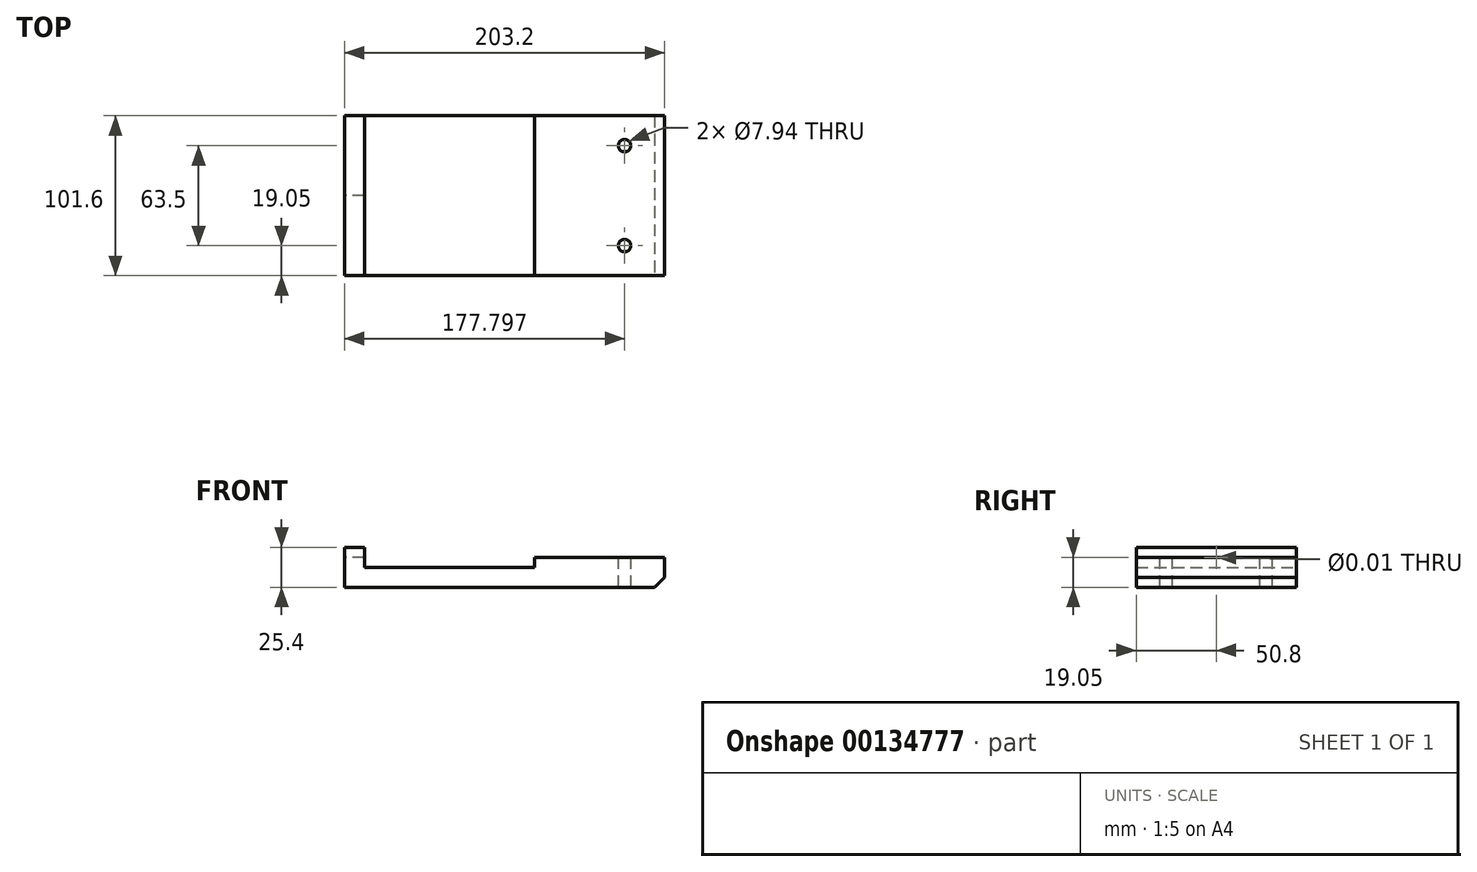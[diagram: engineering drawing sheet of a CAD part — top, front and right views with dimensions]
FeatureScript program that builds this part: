
annotation { "Feature Type Name" : "Feature", "Feature Type Description" : "" }
export const myFeature = defineFeature(function(context is Context, id is Id, definition is map)
    precondition{}
    {
        {
            var Q0;
            Q0=qCreatedBy(makeId("Front.planeOp"),FACE);
            var sketch = newSketch(context, id + "F0", { "sketchPlane" : qUnion([Q0])});
            skLineSegment(sketch, "E0", {"start": v(-106, -12.7) * mm, "end": v(97.2, -12.7) * mm});
            skLineSegment(sketch, "E1", {"start": v(97.2, -12.7) * mm, "end": v(97.2, 6.35) * mm});
            skLineSegment(sketch, "E2", {"start": v(97.2, 6.35) * mm, "end": v(14.65, 6.35) * mm});
            skLineSegment(sketch, "E3", {"start": v(14.65, 6.35) * mm, "end": v(14.65, 0) * mm});
            skLineSegment(sketch, "E4", {"start": v(14.65, 0) * mm, "end": v(-93.3, 0) * mm});
            skLineSegment(sketch, "E5", {"start": v(-93.3, 0) * mm, "end": v(-93.3, 12.7) * mm});
            skLineSegment(sketch, "E6", {"start": v(-93.3, 12.7) * mm, "end": v(-106, 12.7) * mm});
            skLineSegment(sketch, "E7", {"start": v(-106, 12.7) * mm, "end": v(-106, -12.7) * mm});
            skSolve(sketch);
        }
        {
            var Q0;
            Q0=makeQuery(id+"F0.imprint","IMPRINT",FACE,{"disambiguationData":[TD([[makeQuery(id+"F0.imprint","IMPRINT",EDGE,{"derivedFrom":sQuery(id+"F0.wireOp",EDGE,"E0")}),1.0]])]});
            extrude(context, id + "F1", {"entities" : qUnion([Q0]), "endBound" : BoundingType.SYMMETRIC, "depth" : 101.6 * mm});
        }
        {
            var Q0;
            Q0=makeQuery(id+"F1.opExtrude","SWEPT_EDGE",EDGE,{"disambiguationData":[OSD([sQuery(id+"F0.wireOp",EDGE,"E0"),sQuery(id+"F0.wireOp",EDGE,"E1")])]});
            chamfer(context, id + "F2", {"entities" : qUnion([Q0]), "width" : 6.35 * mm, "tangentPropagation" : true});
        }
        {
            var Q0;
            Q0=makeQuery(id+"F1.opExtrude","SWEPT_FACE",FACE,{"disambiguationData":[OSD([sQuery(id+"F0.wireOp",EDGE,"E2")])]});
            var sketch = newSketch(context, id + "F3", { "sketchPlane" : qUnion([Q0])});
            skCircle(sketch, "E8", {"center": v(71.8, 31.75) * mm, "radius": 3.87 * mm});
            skCircle(sketch, "E9.MirrorC", {"center": v(71.8, -31.75) * mm, "radius": 3.87 * mm});
            skSolve(sketch);
        }
        {
            var Q0;
            Q0=sQuery(id+"F3.wireOp",VERTEX,"E8.center");
            var Q1;
            Q1=sQuery(id+"F3.wireOp",VERTEX,"E9.MirrorC.center");
            var Q2;
            Q2=makeQuery(id+"F1.opExtrude","SWEPT_BODY",BODY,{"disambiguationData":[OSD([sQuery(id+"F0.wireOp",EDGE,"E0"),sQuery(id+"F0.wireOp",EDGE,"E1"),sQuery(id+"F0.wireOp",EDGE,"E2"),sQuery(id+"F0.wireOp",EDGE,"E3"),sQuery(id+"F0.wireOp",EDGE,"E4"),sQuery(id+"F0.wireOp",EDGE,"E5"),sQuery(id+"F0.wireOp",EDGE,"E6"),sQuery(id+"F0.wireOp",EDGE,"E7")])]});
            hole(context, id + "F4", {"style" : HoleStyle.SIMPLE, "endStyle" : HoleEndStyle.THROUGH, "standardTappedOrClearance" : lookupTablePath({ "standard" : "ANSI", "engagement" : "75%", "pitch" : "16 tpi", "size" : "3/8", "type" : "Tapped" }), "standardBlindInLast" : lookupTablePath({ "standard" : "ANSI", "engagement" : "75%", "pitch" : "16 tpi", "size" : "3/8", "type" : "Tapped" }), "holeDiameter" : 7.94 * mm, "startFromSketch" : true, "locations" : qUnion([Q0, Q1]), "scope" : qUnion([Q2]), "isTappedThrough" : true, "majorDiameter" : 9.53 * mm, "showTappedDepth" : true});
        }
        {
            var Q0;
            Q0=makeQuery(id+"F1.opExtrude","SWEPT_FACE",FACE,{"disambiguationData":[OSD([sQuery(id+"F0.wireOp",EDGE,"E7")])]});
            var sketch = newSketch(context, id + "F5", { "sketchPlane" : qUnion([Q0])});
            skCircle(sketch, "E10", {"center": v(0, 6.35) * mm, "radius": 4.29 * mm});
            skPoint(sketch, "E10.centerSnap0", {"position": v(0, 12.7) * mm});
            skSolve(sketch);
        }
        {
            var Q0;
            Q0=sQuery(id+"F5.wireOp",VERTEX,"E10.center");
            var Q1;
            Q1=makeQuery(id+"F1.opExtrude","SWEPT_BODY",BODY,{"disambiguationData":[OSD([sQuery(id+"F0.wireOp",EDGE,"E0"),sQuery(id+"F0.wireOp",EDGE,"E1"),sQuery(id+"F0.wireOp",EDGE,"E2"),sQuery(id+"F0.wireOp",EDGE,"E3"),sQuery(id+"F0.wireOp",EDGE,"E4"),sQuery(id+"F0.wireOp",EDGE,"E5"),sQuery(id+"F0.wireOp",EDGE,"E6"),sQuery(id+"F0.wireOp",EDGE,"E7")])]});
            hole(context, id + "F6", {"style" : HoleStyle.SIMPLE, "endStyle" : HoleEndStyle.BLIND, "standardTappedOrClearance" : lookupTablePath({ "standard" : "ANSI", "size" : "3/8 (0.38)", "type" : "Drilled" }), "standardBlindInLast" : lookupTablePath({ "standard" : "ANSI", "size" : "3/8", "type" : "Drilled" }), "holeDiameter" : 3 / 203.2 * mm, "holeDepth" : 19.05 * mm, "startFromSketch" : true, "locations" : qUnion([Q0]), "scope" : qUnion([Q1])});
        }
    });
